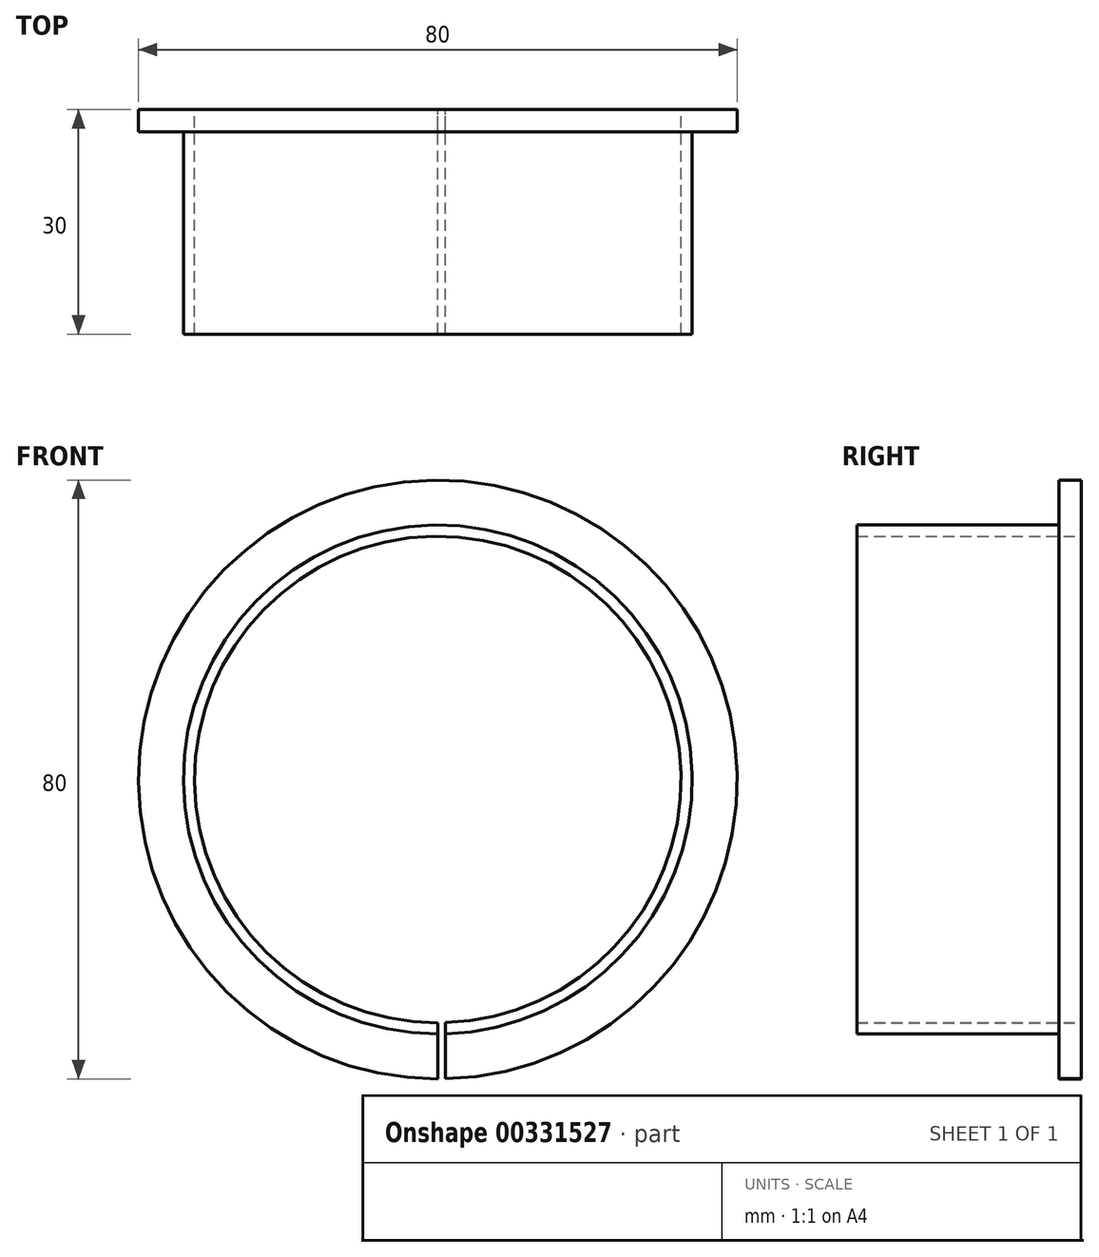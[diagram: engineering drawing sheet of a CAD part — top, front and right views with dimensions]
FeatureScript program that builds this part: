
annotation { "Feature Type Name" : "Feature", "Feature Type Description" : "" }
export const myFeature = defineFeature(function(context is Context, id is Id, definition is map)
    precondition{}
    {
        {
            var Q0;
            Q0=qCreatedBy(makeId("Front.planeOp"),FACE);
            var sketch = newSketch(context, id + "F0", { "sketchPlane" : qUnion([Q0])});
            skCircle(sketch, "E0", {"center": v(-117.9, 35.4) * mm, "radius": 32.5 * mm});
            skCircle(sketch, "E1", {"center": v(-117.9, 35.4) * mm, "radius": 34 * mm});
            skCircle(sketch, "E2", {"center": v(-117.9, 35.4) * mm, "radius": 40 * mm});
            skSolve(sketch);
        }
        {
            var Q0;
            Q0 = qSketchRegion(id + "F0", true);
            var Q1;
            Q1=makeQuery(id+"F0.imprint","IMPRINT",FACE,{"disambiguationData":[TD([[makeQuery(id+"F0.imprint","IMPRINT",EDGE,{"derivedFrom":sQuery(id+"F0.wireOp",EDGE,"E0")}),-1.0]])]});
            extrude(context, id + "F1", {"entities" : qUnion([Q0, Q1]), "depth" : 3 * mm});
        }
        {
            var Q0;
            Q0=makeQuery(id+"F1.opExtrude","CAP_FACE",FACE,{"disambiguationData":[OSD([sQuery(id+"F0.wireOp",EDGE,"E0"),sQuery(id+"F0.wireOp",EDGE,"E2")])],"isStart":false});
            var sketch = newSketch(context, id + "F2", { "sketchPlane" : qUnion([Q0])});
            skCircle(sketch, "E3", {"center": v(-117.9, 35.4) * mm, "radius": 32.5 * mm});
            skCircle(sketch, "E4", {"center": v(-117.9, 35.4) * mm, "radius": 34 * mm});
            skSolve(sketch);
        }
        {
            var Q0;
            Q0 = qSketchRegion(id + "F2", true);
            extrude(context, id + "F3", {"entities" : qUnion([Q0]), "operationType" : NewBodyOperationType.ADD, "depth" : 27 * mm});
        }
        {
            var Q0;
            Q0=makeQuery(id+"F3.opExtrude","CAP_FACE",FACE,{"disambiguationData":[OSD([sQuery(id+"F2.wireOp",EDGE,"E3"),sQuery(id+"F2.wireOp",EDGE,"E4")])],"isStart":false});
            var sketch = newSketch(context, id + "F4", { "sketchPlane" : qUnion([Q0])});
            skLineSegment(sketch, "E5.bottom", {"start": v(-117.9, 35.4) * mm, "end": v(-116.9, 35.4) * mm});
            skLineSegment(sketch, "E5.top", {"start": v(-117.9, -10.6) * mm, "end": v(-116.9, -10.6) * mm});
            skLineSegment(sketch, "E5.left", {"start": v(-117.9, 35.4) * mm, "end": v(-117.9, -10.6) * mm});
            skLineSegment(sketch, "E5.right", {"start": v(-116.9, 35.4) * mm, "end": v(-116.9, -10.6) * mm});
            skSolve(sketch);
        }
        {
            var Q0;
            Q0 = qSketchRegion(id + "F4", true);
            extrude(context, id + "F5", {"entities" : qUnion([Q0]), "operationType" : NewBodyOperationType.REMOVE, "oppositeDirection" : true, "depth" : 56.9 * mm});
        }
    });
